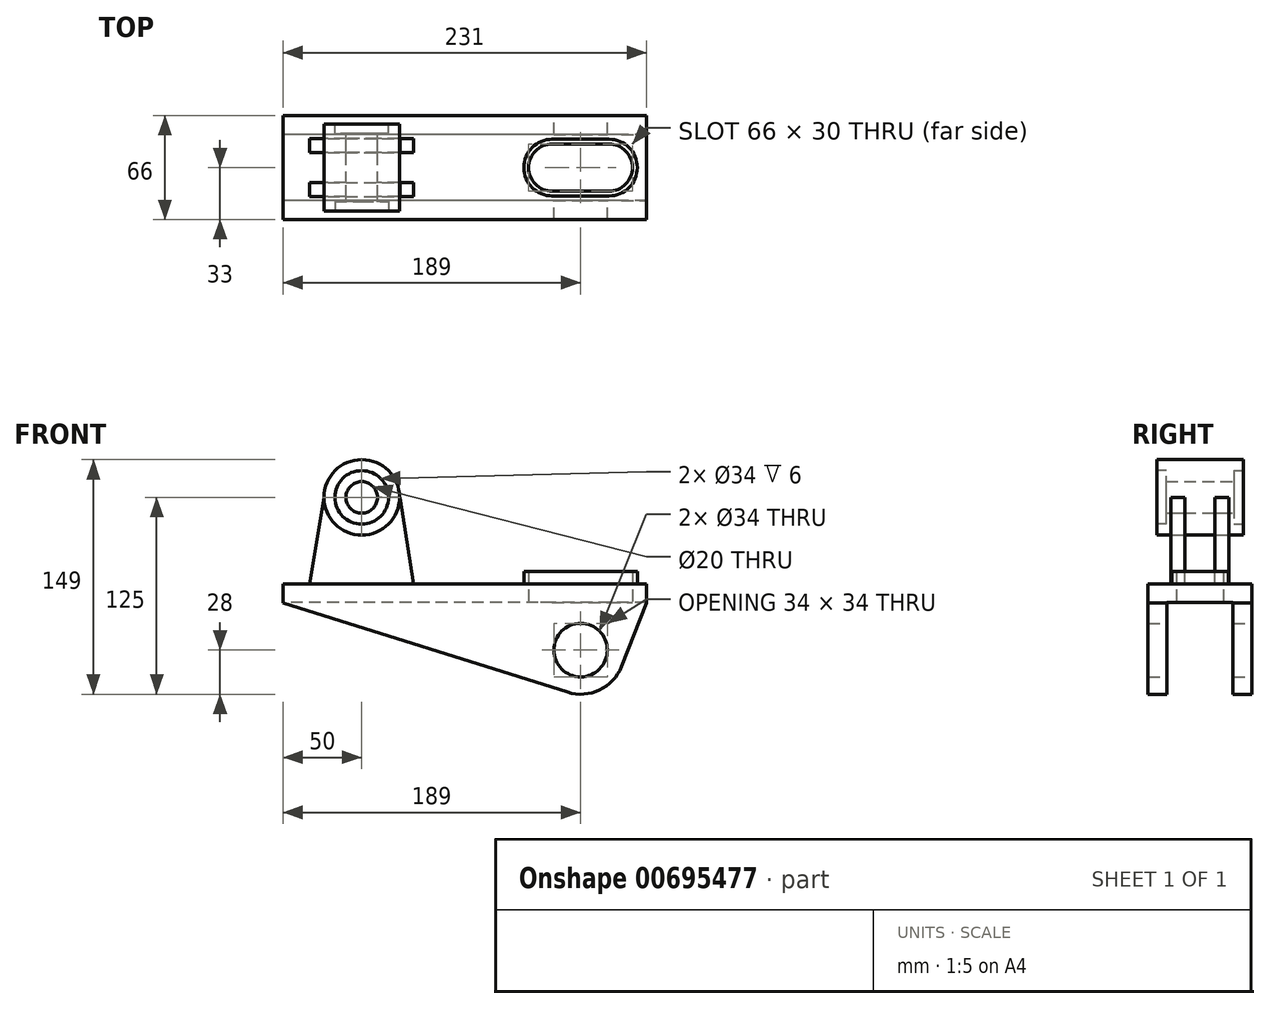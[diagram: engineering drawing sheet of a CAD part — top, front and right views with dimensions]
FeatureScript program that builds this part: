
annotation { "Feature Type Name" : "Feature", "Feature Type Description" : "" }
export const myFeature = defineFeature(function(context is Context, id is Id, definition is map)
    precondition{}
    {
        {
            var Q0;
            Q0=qCreatedBy(makeId("Top.planeOp"),FACE);
            var sketch = newSketch(context, id + "F0", { "sketchPlane" : qUnion([Q0])});
            skLineSegment(sketch, "E0.bottom", {"start": v(-115.5, 33) * mm, "end": v(115.5, 33) * mm});
            skLineSegment(sketch, "E0.top", {"start": v(-115.5, -33) * mm, "end": v(115.5, -33) * mm});
            skLineSegment(sketch, "E0.left", {"start": v(-115.5, 33) * mm, "end": v(-115.5, -33) * mm});
            skLineSegment(sketch, "E0.right", {"start": v(115.5, 33) * mm, "end": v(115.5, -33) * mm});
            skPoint(sketch, "E0.middle", {"position": v(0, 0) * mm});
            skSolve(sketch);
        }
        {
            var Q0;
            Q0=makeQuery(id+"F0.imprint","IMPRINT",FACE,{"disambiguationData":[TD([[makeQuery(id+"F0.imprint","IMPRINT",EDGE,{"derivedFrom":sQuery(id+"F0.wireOp",EDGE,"E0.bottom")}),-1.0]])]});
            extrude(context, id + "F1", {"entities" : qUnion([Q0]), "oppositeDirection" : true, "depth" : 12 * mm, "offsetDistance" : 25 * mm});
        }
        {
            var Q0;
            Q0=makeQuery(id+"F1.opExtrude","CAP_FACE",FACE,{"disambiguationData":[OSD([sQuery(id+"F0.wireOp",EDGE,"E0.bottom"),sQuery(id+"F0.wireOp",EDGE,"E0.top"),sQuery(id+"F0.wireOp",EDGE,"E0.left"),sQuery(id+"F0.wireOp",EDGE,"E0.right")])],"isStart":true});
            var sketch = newSketch(context, id + "F2", { "sketchPlane" : qUnion([Q0])});
            skPoint(sketch, "E1.middle", {"position": v(73.5, 0) * mm});
            skLineSegment(sketch, "E2.bottom", {"start": v(55.5, 15) * mm, "end": v(91.5, 15) * mm});
            skLineSegment(sketch, "E2.top", {"start": v(55.5, -15) * mm, "end": v(91.5, -15) * mm});
            skArc(sketch, "E3", {"start": v(55.5, 15) * mm, "mid": v(40.5, 0) * mm, "end": v(55.5, -15) * mm});
            skArc(sketch, "E4", {"start": v(91.5, -15) * mm, "mid": v(106.5, 0) * mm, "end": v(91.5, 15) * mm});
            skLineSegment(sketch, "E5.bottom", {"start": v(55.5, 18) * mm, "end": v(91.5, 18) * mm});
            skLineSegment(sketch, "E5.top", {"start": v(55.5, -18) * mm, "end": v(91.5, -18) * mm});
            skArc(sketch, "E6", {"start": v(55.5, 18) * mm, "mid": v(37.5, 0) * mm, "end": v(55.5, -18) * mm});
            skArc(sketch, "E7", {"start": v(91.5, -18) * mm, "mid": v(109.5, 0) * mm, "end": v(91.5, 18) * mm});
            skSolve(sketch);
        }
        {
            var Q0;
            Q0=makeQuery(id+"F2.imprint","IMPRINT",FACE,{"disambiguationData":[TD([[makeQuery(id+"F2.imprint","IMPRINT",EDGE,{"derivedFrom":sQuery(id+"F2.wireOp",EDGE,"E2.bottom")}),1.0]])]});
            extrude(context, id + "F3", {"entities" : qUnion([Q0]), "operationType" : NewBodyOperationType.ADD, "depth" : 8 * mm, "offsetDistance" : 25 * mm});
        }
        {
            var Q0;
            Q0=makeQuery(id+"F2.imprint","IMPRINT",FACE,{"disambiguationData":[TD([[makeQuery(id+"F2.imprint","IMPRINT",EDGE,{"derivedFrom":sQuery(id+"F2.wireOp",EDGE,"E2.bottom")}),-1.0]])]});
            extrude(context, id + "F4", {"entities" : qUnion([Q0]), "operationType" : NewBodyOperationType.REMOVE, "endBound" : BoundingType.THROUGH_ALL, "oppositeDirection" : true, "depth" : 25 * mm, "offsetDistance" : 25 * mm});
        }
        {
            var Q0;
            Q0=qCreatedBy(makeId("Front.planeOp"),FACE);
            var sketch = newSketch(context, id + "F5", { "sketchPlane" : qUnion([Q0])});
            skCircle(sketch, "E8", {"center": v(-65.5, 55) * mm, "radius": 24 * mm});
            skSolve(sketch);
        }
        {
            var Q0;
            Q0=makeQuery(id+"F5.imprint","IMPRINT",FACE,{"disambiguationData":[TD([[makeQuery(id+"F5.imprint","IMPRINT",EDGE,{"derivedFrom":sQuery(id+"F5.wireOp",EDGE,"E8")}),1.0]])]});
            extrude(context, id + "F6", {"entities" : qUnion([Q0]), "depth" : 55 * mm, "offsetDistance" : 25 * mm, "symmetric" : true});
        }
        {
            var Q0;
            Q0=makeQuery(id+"F6.opExtrude","CAP_FACE",FACE,{"disambiguationData":[OSD([sQuery(id+"F5.wireOp",EDGE,"E8")])],"isStart":false});
            cPlane(context, id + "F7", {"entities" : qUnion([Q0]), "cplaneType" : CPlaneType.OFFSET, "offset" : 9 * mm, "oppositeDirection" : true, "width" : 150 * mm, "height" : 150 * mm});
        }
        {
            var Q0;
            Q0=qCreatedBy(id+"F7.planeOp",FACE);
            var sketch = newSketch(context, id + "F8", { "sketchPlane" : qUnion([Q0])});
            skCircle(sketch, "E9.0.0", {"center": v(-65.5, 55) * mm, "radius": 24 * mm, "construction": true});
            skLineSegment(sketch, "E10", {"start": v(-65.5, 55) * mm, "end": v(-65.5, 0) * mm, "construction": true});
            skPoint(sketch, "E11", {"position": v(-98.5, 0) * mm});
            skLineSegment(sketch, "E12", {"start": v(-98.5, 0) * mm, "end": v(-89.5, 55) * mm});
            skPoint(sketch, "E13", {"position": v(-32.5, 0) * mm});
            skLineSegment(sketch, "E14", {"start": v(-32.5, 0) * mm, "end": v(-41.2, 55) * mm});
            skLineSegment(sketch, "E15", {"start": v(-41.2, 55) * mm, "end": v(-89.5, 55) * mm});
            skLineSegment(sketch, "E16", {"start": v(-98.5, 0) * mm, "end": v(-32.5, 0) * mm});
            skSolve(sketch);
        }
        {
            var Q0;
            Q0=makeQuery(id+"F8.imprint","IMPRINT",FACE,{"disambiguationData":[TD([[makeQuery(id+"F8.imprint","IMPRINT",EDGE,{"derivedFrom":sQuery(id+"F8.wireOp",EDGE,"E12")}),-1.0]])]});
            extrude(context, id + "F9", {"entities" : qUnion([Q0]), "oppositeDirection" : true, "depth" : 9 * mm, "offsetDistance" : 25 * mm});
        }
        {
            var Q0;
            Q0=makeQuery(id+"F6.opExtrude","CAP_FACE",FACE,{"disambiguationData":[OSD([sQuery(id+"F5.wireOp",EDGE,"E8")])],"isStart":true});
            cPlane(context, id + "F10", {"entities" : qUnion([Q0]), "cplaneType" : CPlaneType.OFFSET, "offset" : 9 * mm, "oppositeDirection" : true, "width" : 150 * mm, "height" : 150 * mm});
        }
        {
            var Q0;
            Q0=qCreatedBy(id+"F10.planeOp",FACE);
            var sketch = newSketch(context, id + "F11", { "sketchPlane" : qUnion([Q0])});
            skLineSegment(sketch, "E17", {"start": v(65.5, 55) * mm, "end": v(65.5, 0) * mm, "construction": true});
            skPoint(sketch, "E18", {"position": v(32.5, 0) * mm});
            skPoint(sketch, "E19", {"position": v(98.5, 0) * mm});
            skLineSegment(sketch, "E20", {"start": v(32.5, 0) * mm, "end": v(41.2, 55) * mm});
            skLineSegment(sketch, "E21", {"start": v(41.2, 55) * mm, "end": v(89.5, 55) * mm});
            skLineSegment(sketch, "E22", {"start": v(89.5, 55) * mm, "end": v(98.5, 0) * mm});
            skLineSegment(sketch, "E23", {"start": v(98.5, 0) * mm, "end": v(32.5, 0) * mm});
            skSolve(sketch);
        }
        {
            var Q0;
            Q0=makeQuery(id+"F11.imprint","IMPRINT",FACE,{"disambiguationData":[TD([[makeQuery(id+"F11.imprint","IMPRINT",EDGE,{"derivedFrom":sQuery(id+"F11.wireOp",EDGE,"E20")}),-1.0]])]});
            extrude(context, id + "F12", {"entities" : qUnion([Q0]), "oppositeDirection" : true, "depth" : 9 * mm, "offsetDistance" : 25 * mm});
        }
        {
            var Q0;
            Q0=makeQuery(id+"F6.opExtrude","CAP_FACE",FACE,{"disambiguationData":[OSD([sQuery(id+"F5.wireOp",EDGE,"E8")])],"isStart":true});
            var sketch = newSketch(context, id + "F13", { "sketchPlane" : qUnion([Q0])});
            skCircle(sketch, "E24", {"center": v(65.5, 55) * mm, "radius": 10 * mm});
            skSolve(sketch);
        }
        {
            var Q0;
            Q0=makeQuery(id+"F13.imprint","IMPRINT",FACE,{"disambiguationData":[TD([[makeQuery(id+"F13.imprint","IMPRINT",EDGE,{"derivedFrom":sQuery(id+"F13.wireOp",EDGE,"E24")}),1.0]])]});
            extrude(context, id + "F14", {"entities" : qUnion([Q0]), "operationType" : NewBodyOperationType.REMOVE, "endBound" : BoundingType.THROUGH_ALL, "oppositeDirection" : true, "depth" : 34.6 * mm, "offsetDistance" : 25 * mm});
        }
        {
            var Q0;
            Q0=makeQuery(id+"F6.opExtrude","CAP_FACE",FACE,{"disambiguationData":[OSD([sQuery(id+"F5.wireOp",EDGE,"E8")])],"isStart":true});
            var sketch = newSketch(context, id + "F15", { "sketchPlane" : qUnion([Q0])});
            skCircle(sketch, "E25", {"center": v(65.5, 55) * mm, "radius": 17 * mm});
            skSolve(sketch);
        }
        {
            var Q0;
            Q0=makeQuery(id+"F15.imprint","IMPRINT",FACE,{"disambiguationData":[TD([[makeQuery(id+"F15.imprint","IMPRINT",EDGE,{"derivedFrom":sQuery(id+"F15.wireOp",EDGE,"E25")}),1.0]])]});
            extrude(context, id + "F16", {"entities" : qUnion([Q0]), "operationType" : NewBodyOperationType.REMOVE, "oppositeDirection" : true, "depth" : 6 * mm, "offsetDistance" : 25 * mm});
        }
        {
            var Q0;
            Q0=makeQuery(id+"F6.opExtrude","CAP_FACE",FACE,{"disambiguationData":[OSD([sQuery(id+"F5.wireOp",EDGE,"E8")])],"isStart":false});
            var sketch = newSketch(context, id + "F17", { "sketchPlane" : qUnion([Q0])});
            skCircle(sketch, "E26", {"center": v(-65.5, 55) * mm, "radius": 17 * mm});
            skSolve(sketch);
        }
        {
            var Q0;
            Q0=makeQuery(id+"F17.imprint","IMPRINT",FACE,{"disambiguationData":[TD([[makeQuery(id+"F17.imprint","IMPRINT",EDGE,{"derivedFrom":sQuery(id+"F17.wireOp",EDGE,"E26")}),1.0]])]});
            extrude(context, id + "F18", {"entities" : qUnion([Q0]), "operationType" : NewBodyOperationType.REMOVE, "oppositeDirection" : true, "depth" : 6 * mm, "offsetDistance" : 25 * mm});
        }
        {
            var Q0;
            Q0=qCreatedBy(makeId("Front.planeOp"),FACE);
            var sketch = newSketch(context, id + "F19", { "sketchPlane" : qUnion([Q0])});
            skArc(sketch, "E27", {"start": v(65.11, -68.71) * mm, "mid": v(85.55, -67.28) * mm, "end": v(99.53, -52.31) * mm});
            skPoint(sketch, "E28.0", {"position": v(115.5, -12) * mm});
            skLineSegment(sketch, "E29", {"start": v(115.5, -12) * mm, "end": v(99.53, -52.31) * mm});
            skPoint(sketch, "E30.0", {"position": v(-115.5, -12) * mm});
            skLineSegment(sketch, "E31", {"start": v(-115.5, -12) * mm, "end": v(65.11, -68.71) * mm});
            skCircle(sketch, "E32", {"center": v(73.5, -42) * mm, "radius": 17 * mm});
            skLineSegment(sketch, "E33", {"start": v(-115.5, -12) * mm, "end": v(115.5, -12) * mm});
            skSolve(sketch);
        }
        {
            var Q0;
            Q0=makeQuery(id+"F19.imprint","IMPRINT",FACE,{"disambiguationData":[TD([[makeQuery(id+"F19.imprint","IMPRINT",EDGE,{"derivedFrom":sQuery(id+"F19.wireOp",EDGE,"E27")}),1.0]])]});
            extrude(context, id + "F20", {"entities" : qUnion([Q0]), "operationType" : NewBodyOperationType.ADD, "depth" : 66 * mm, "offsetDistance" : 25 * mm, "symmetric" : true});
        }
        {
            var Q0;
            Q0=qCreatedBy(makeId("Right.planeOp"),FACE);
            var sketch = newSketch(context, id + "F21", { "sketchPlane" : qUnion([Q0])});
            skLineSegment(sketch, "E34.bottom", {"start": v(-21, -11.63) * mm, "end": v(21, -11.63) * mm});
            skLineSegment(sketch, "E34.top", {"start": v(-21, -76.67) * mm, "end": v(21, -76.67) * mm});
            skLineSegment(sketch, "E34.left", {"start": v(-21, -11.63) * mm, "end": v(-21, -76.67) * mm});
            skLineSegment(sketch, "E34.right", {"start": v(21, -11.63) * mm, "end": v(21, -76.67) * mm});
            skSolve(sketch);
        }
        {
            var Q0;
            Q0=makeQuery(id+"F21.imprint","IMPRINT",FACE,{"disambiguationData":[TD([[makeQuery(id+"F21.imprint","IMPRINT",EDGE,{"derivedFrom":sQuery(id+"F21.wireOp",EDGE,"E34.bottom")}),-1.0]])]});
            extrude(context, id + "F22", {"entities" : qUnion([Q0]), "operationType" : NewBodyOperationType.REMOVE, "endBound" : BoundingType.THROUGH_ALL, "depth" : 25 * mm, "offsetDistance" : 25 * mm, "hasSecondDirection" : true, "secondDirectionBound" : BoundingType.THROUGH_ALL, "secondDirectionOppositeDirection" : true, "secondDirectionDepth" : 25 * mm});
        }
    });
